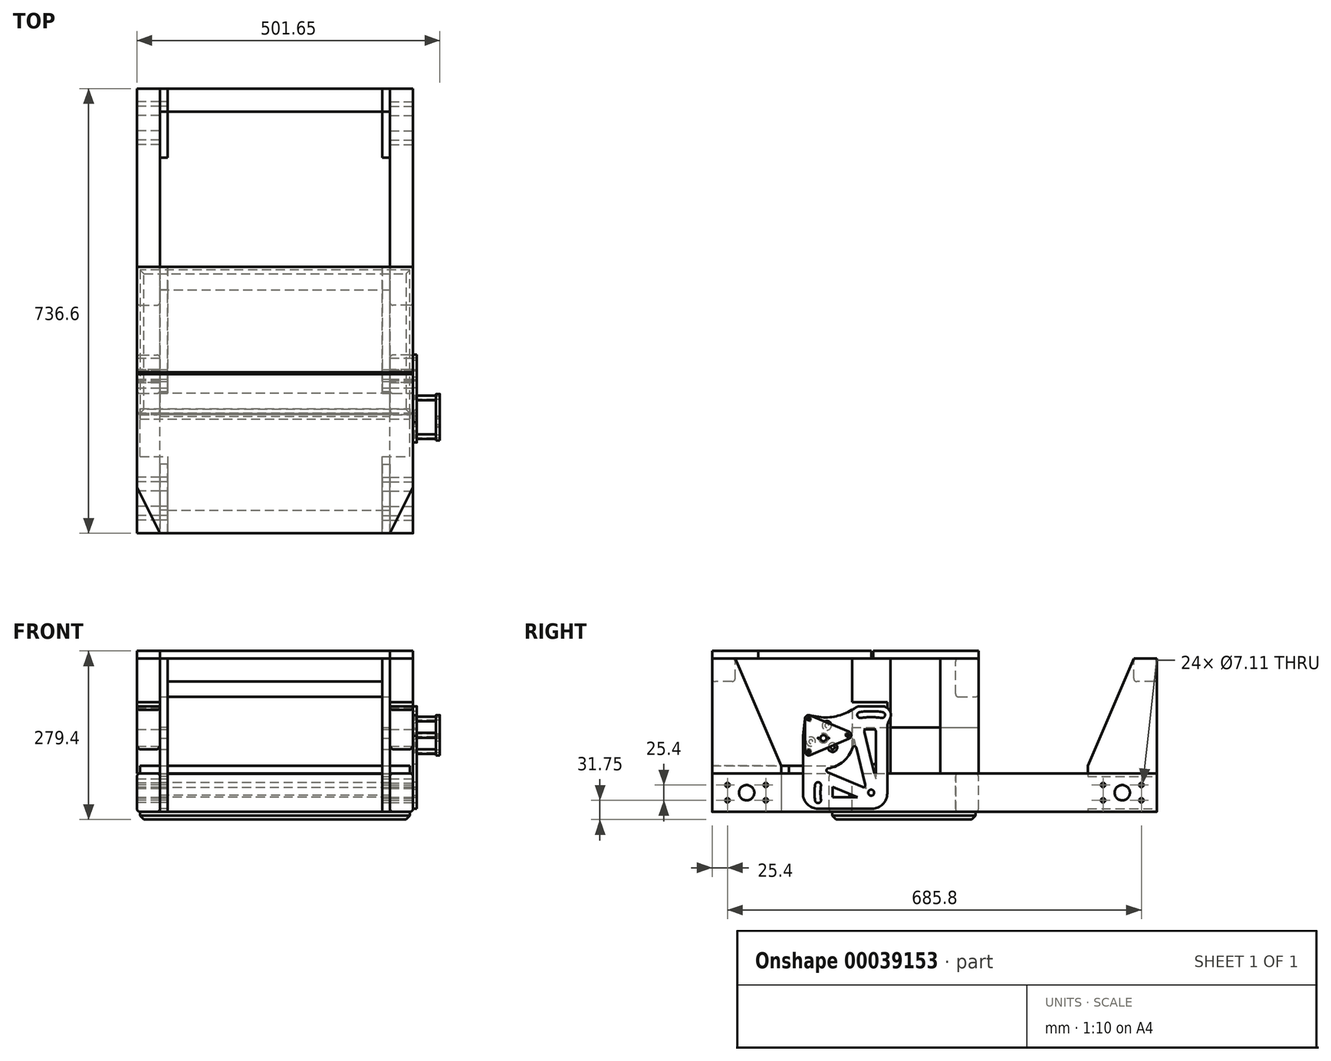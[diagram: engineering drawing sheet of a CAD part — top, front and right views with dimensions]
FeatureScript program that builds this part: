
annotation { "Feature Type Name" : "Feature", "Feature Type Description" : "" }
export const myFeature = defineFeature(function(context is Context, id is Id, definition is map)
    precondition{}
    {
        {
            var Q0;
            Q0=qCreatedBy(makeId("Front.planeOp"),FACE);
            var sketch = newSketch(context, id + "F0", { "sketchPlane" : qUnion([Q0])});
            skLineSegment(sketch, "E0", {"start": v(0, 25.4) * mm, "end": v(0, -25.4) * mm, "construction": true});
            skLineSegment(sketch, "E1.rect.bottom", {"start": v(-190.5, 31.75) * mm, "end": v(-228.6, 31.75) * mm});
            skLineSegment(sketch, "E1.rect.top", {"start": v(-190.5, -31.75) * mm, "end": v(-228.6, -31.75) * mm});
            skLineSegment(sketch, "E1.rect.left", {"start": v(-190.5, 31.75) * mm, "end": v(-190.5, -31.75) * mm});
            skLineSegment(sketch, "E1.rect.right", {"start": v(-228.6, 31.75) * mm, "end": v(-228.6, -31.75) * mm});
            skPoint(sketch, "E1.rect.middle", {"position": v(-209.55, 0) * mm});
            skLineSegment(sketch, "E2.MirrorCS", {"start": v(190.5, 31.75) * mm, "end": v(228.6, 31.75) * mm});
            skLineSegment(sketch, "E3.MirrorCS", {"start": v(190.5, -31.75) * mm, "end": v(228.6, -31.75) * mm});
            skLineSegment(sketch, "E4.MirrorCS", {"start": v(228.6, 31.75) * mm, "end": v(228.6, -31.75) * mm});
            skLineSegment(sketch, "E5.MirrorCS", {"start": v(190.5, 31.75) * mm, "end": v(190.5, -31.75) * mm});
            skPoint(sketch, "E6.MirrorP", {"position": v(209.55, 0) * mm});
            skSolve(sketch);
        }
        {
            var Q0;
            Q0=makeQuery(id+"F0.imprint","IMPRINT",FACE,{"disambiguationData":[TD([[makeQuery(id+"F0.imprint","IMPRINT",EDGE,{"derivedFrom":sQuery(id+"F0.wireOp",EDGE,"E1.rect.bottom")}),1.0]])]});
            extrude(context, id + "F1", {"entities" : qUnion([Q0]), "endBound" : BoundingType.SYMMETRIC, "depth" : 736.6 * mm});
        }
        {
            var Q0;
            Q0=makeQuery(id+"F1.opExtrude","SWEPT_FACE",FACE,{"disambiguationData":[OSD([sQuery(id+"F0.wireOp",EDGE,"E1.rect.right")])]});
            var sketch = newSketch(context, id + "F2", { "sketchPlane" : qUnion([Q0])});
            skLineSegment(sketch, "E7.rect.bottom", {"start": v(342.9, -12.7) * mm, "end": v(279.4, -12.7) * mm, "construction": true});
            skLineSegment(sketch, "E7.rect.top", {"start": v(342.9, 12.7) * mm, "end": v(279.4, 12.7) * mm, "construction": true});
            skLineSegment(sketch, "E7.rect.left", {"start": v(342.9, -12.7) * mm, "end": v(342.9, 12.7) * mm, "construction": true});
            skLineSegment(sketch, "E7.rect.right", {"start": v(279.4, -12.7) * mm, "end": v(279.4, 12.7) * mm, "construction": true});
            skPoint(sketch, "E7.rect.middle", {"position": v(311.15, 0) * mm});
            skCircle(sketch, "E8", {"center": v(311.15, 0) * mm, "radius": 12.7 * mm});
            skCircle(sketch, "E9", {"center": v(279.4, 12.7) * mm, "radius": 3.56 * mm});
            skCircle(sketch, "E10", {"center": v(279.4, -12.7) * mm, "radius": 3.56 * mm});
            skCircle(sketch, "E11", {"center": v(342.9, -12.7) * mm, "radius": 3.56 * mm});
            skCircle(sketch, "E12", {"center": v(342.9, 12.7) * mm, "radius": 3.56 * mm});
            skLineSegment(sketch, "E13", {"start": v(0, 31.75) * mm, "end": v(0, -31.75) * mm, "construction": true});
            skCircle(sketch, "E14.MirrorC", {"center": v(-342.9, 12.7) * mm, "radius": 3.56 * mm});
            skCircle(sketch, "E15.MirrorC", {"center": v(-342.9, -12.7) * mm, "radius": 3.56 * mm});
            skCircle(sketch, "E16.MirrorC", {"center": v(-279.4, 12.7) * mm, "radius": 3.56 * mm});
            skCircle(sketch, "E17.MirrorC", {"center": v(-279.4, -12.7) * mm, "radius": 3.56 * mm});
            skCircle(sketch, "E18.MirrorC", {"center": v(-311.15, 0) * mm, "radius": 12.7 * mm});
            skSolve(sketch);
        }
        {
            var Q0;
            Q0 = qSketchRegion(id + "F2", true);
            extrude(context, id + "F3", {"entities" : qUnion([Q0]), "operationType" : NewBodyOperationType.REMOVE, "endBound" : BoundingType.THROUGH_ALL, "oppositeDirection" : true, "depth" : 25.4 * mm});
        }
        {
            var Q0;
            Q0=makeQuery(id+"F1.opExtrude","SWEPT_EDGE",EDGE,{"disambiguationData":[OSD([sQuery(id+"F0.wireOp",EDGE,"E1.rect.bottom"),sQuery(id+"F0.wireOp",EDGE,"E1.rect.right")])]});
            var Q1;
            Q1=makeQuery(id+"F1.opExtrude","SWEPT_EDGE",EDGE,{"disambiguationData":[OSD([sQuery(id+"F0.wireOp",EDGE,"E1.rect.bottom"),sQuery(id+"F0.wireOp",EDGE,"E1.rect.left")])]});
            var Q2;
            Q2=makeQuery(id+"F1.opExtrude","SWEPT_EDGE",EDGE,{"disambiguationData":[OSD([sQuery(id+"F0.wireOp",EDGE,"E1.rect.top"),sQuery(id+"F0.wireOp",EDGE,"E1.rect.right")])]});
            var Q3;
            Q3=makeQuery(id+"F1.opExtrude","SWEPT_EDGE",EDGE,{"disambiguationData":[OSD([sQuery(id+"F0.wireOp",EDGE,"E1.rect.top"),sQuery(id+"F0.wireOp",EDGE,"E1.rect.left")])]});
            fillet(context, id + "F4", {"entities" : qUnion([Q0, Q1, Q2, Q3]), "radius" : 5.08 * mm, "tangentPropagation" : true, "allowEdgeOverflow" : false});
        }
        {
            var Q0;
            Q0=makeQuery(id+"F1.opExtrude","SWEPT_BODY",BODY,{"disambiguationData":[OSD([sQuery(id+"F0.wireOp",EDGE,"E1.rect.bottom"),sQuery(id+"F0.wireOp",EDGE,"E1.rect.top"),sQuery(id+"F0.wireOp",EDGE,"E1.rect.left"),sQuery(id+"F0.wireOp",EDGE,"E1.rect.right")])]});
            var Q1;
            Q1=qCreatedBy(makeId("Right.planeOp"),FACE);
            mirror(context, id + "F5", {"entities" : qUnion([Q0]), "mirrorPlane" : qUnion([Q1])});
        }
        {
            var Q0;
            Q0=makeQuery(id+"F1.opExtrude","SWEPT_FACE",FACE,{"disambiguationData":[OSD([sQuery(id+"F0.wireOp",EDGE,"E1.rect.bottom")])]});
            var sketch = newSketch(context, id + "F6", { "sketchPlane" : qUnion([Q0])});
            skLineSegment(sketch, "E19.bottom", {"start": v(-190.5, -174.62) * mm, "end": v(190.5, -174.62) * mm});
            skLineSegment(sketch, "E19.top", {"start": v(-190.5, -136.53) * mm, "end": v(190.5, -136.53) * mm});
            skLineSegment(sketch, "E19.left", {"start": v(-190.5, -174.62) * mm, "end": v(-190.5, -136.53) * mm});
            skLineSegment(sketch, "E19.right", {"start": v(190.5, -174.62) * mm, "end": v(190.5, -136.53) * mm});
            skLineSegment(sketch, "E20", {"start": v(-190.5, -50.8) * mm, "end": v(190.5, -50.8) * mm, "construction": true});
            skLineSegment(sketch, "E21.MirrorCS", {"start": v(-190.5, 73.02) * mm, "end": v(190.5, 73.02) * mm});
            skLineSegment(sketch, "E22.MirrorCS", {"start": v(-190.5, 34.92) * mm, "end": v(190.5, 34.92) * mm});
            skLineSegment(sketch, "E23.MirrorCS", {"start": v(190.5, 73.02) * mm, "end": v(190.5, 34.92) * mm});
            skLineSegment(sketch, "E24.MirrorCS", {"start": v(-190.5, 73.02) * mm, "end": v(-190.5, 34.92) * mm});
            skSolve(sketch);
        }
        {
            var Q0;
            Q0 = qSketchRegion(id + "F6", true);
            var Q1;
            Q1=makeQuery(id+"F5.opPattern","COPY",FACE,{"derivedFrom":makeQuery(id+"F1.opExtrude","SWEPT_FACE",FACE,{"disambiguationData":[OSD([sQuery(id+"F0.wireOp",EDGE,"E1.rect.top")])]}),"instanceName":"1"});
            extrude(context, id + "F7", {"entities" : qUnion([Q0]), "endBound" : BoundingType.UP_TO_SURFACE, "oppositeDirection" : true, "endBoundEntityFace" : qUnion([Q1]), "depth" : 25.4 * mm});
        }
        {
            var Q0;
            Q0=makeQuery(id+"F7.opExtrude","CAP_EDGE",EDGE,{"disambiguationData":[OSD([sQuery(id+"F6.wireOp",EDGE,"E21.MirrorCS")])],"isStart":false});
            var Q1;
            Q1=makeQuery(id+"F7.opExtrude","CAP_EDGE",EDGE,{"disambiguationData":[OSD([sQuery(id+"F6.wireOp",EDGE,"E22.MirrorCS")])],"isStart":false});
            var Q2;
            Q2=makeQuery(id+"F7.opExtrude","CAP_EDGE",EDGE,{"disambiguationData":[OSD([sQuery(id+"F6.wireOp",EDGE,"E19.top")])],"isStart":false});
            var Q3;
            Q3=makeQuery(id+"F7.opExtrude","CAP_EDGE",EDGE,{"disambiguationData":[OSD([sQuery(id+"F6.wireOp",EDGE,"E19.bottom")])],"isStart":false});
            var Q4;
            Q4=makeQuery(id+"F7.opExtrude","CAP_EDGE",EDGE,{"disambiguationData":[OSD([sQuery(id+"F6.wireOp",EDGE,"E19.bottom")])],"isStart":true});
            var Q5;
            Q5=makeQuery(id+"F7.opExtrude","CAP_EDGE",EDGE,{"disambiguationData":[OSD([sQuery(id+"F6.wireOp",EDGE,"E19.top")])],"isStart":true});
            var Q6;
            Q6=makeQuery(id+"F7.opExtrude","CAP_EDGE",EDGE,{"disambiguationData":[OSD([sQuery(id+"F6.wireOp",EDGE,"E22.MirrorCS")])],"isStart":true});
            var Q7;
            Q7=makeQuery(id+"F7.opExtrude","CAP_EDGE",EDGE,{"disambiguationData":[OSD([sQuery(id+"F6.wireOp",EDGE,"E21.MirrorCS")])],"isStart":true});
            fillet(context, id + "F8", {"entities" : qUnion([Q0, Q1, Q2, Q3, Q4, Q5, Q6, Q7]), "radius" : 5.08 * mm, "tangentPropagation" : true, "allowEdgeOverflow" : false});
        }
        {
            var Q0;
            Q0=makeQuery(id+"F1.opExtrude","SWEPT_FACE",FACE,{"disambiguationData":[OSD([sQuery(id+"F0.wireOp",EDGE,"E1.rect.bottom")])]});
            var sketch = newSketch(context, id + "F9", { "sketchPlane" : qUnion([Q0])});
            skLineSegment(sketch, "E25.bottom", {"start": v(-223.52, -241.3) * mm, "end": v(-177.8, -241.3) * mm});
            skLineSegment(sketch, "E25.top", {"start": v(-223.52, -141.6) * mm, "end": v(223.52, -141.6) * mm});
            skLineSegment(sketch, "E25.left", {"start": v(-223.52, -241.3) * mm, "end": v(-223.52, -141.6) * mm});
            skLineSegment(sketch, "E25.right", {"start": v(223.52, -241.3) * mm, "end": v(223.52, -141.6) * mm});
            skLineSegment(sketch, "E26.0", {"start": v(190.5, -141.6) * mm, "end": v(-190.5, -141.6) * mm, "construction": true});
            skLineSegment(sketch, "E27", {"start": v(-177.8, -241.3) * mm, "end": v(-177.8, -368.3) * mm});
            skLineSegment(sketch, "E28", {"start": v(-177.8, -368.3) * mm, "end": v(177.8, -368.3) * mm});
            skLineSegment(sketch, "E29", {"start": v(177.8, -368.3) * mm, "end": v(177.8, -241.3) * mm});
            skLineSegment(sketch, "E30", {"start": v(0, -141.6) * mm, "end": v(0, -368.3) * mm, "construction": true});
            skLineSegment(sketch, "E31.trimOffspring", {"start": v(177.8, -241.3) * mm, "end": v(223.52, -241.3) * mm});
            skSolve(sketch);
        }
        {
            var Q0;
            Q0 = qSketchRegion(id + "F9", true);
            extrude(context, id + "F10", {"entities" : qUnion([Q0]), "depth" : 12.7 * mm});
        }
        {
            var Q0;
            Q0=makeQuery(id+"F5.opPattern","COPY",FACE,{"derivedFrom":makeQuery(id+"F1.opExtrude","SWEPT_FACE",FACE,{"disambiguationData":[OSD([sQuery(id+"F0.wireOp",EDGE,"E1.rect.top")])]}),"instanceName":"1"});
            var sketch = newSketch(context, id + "F11", { "sketchPlane" : qUnion([Q0])});
            skLineSegment(sketch, "E32.bottom", {"start": v(223.52, 169.55) * mm, "end": v(-223.52, 169.54) * mm});
            skLineSegment(sketch, "E32.top", {"start": v(223.52, -67.94) * mm, "end": v(-223.52, -67.95) * mm});
            skLineSegment(sketch, "E32.left", {"start": v(223.52, 169.55) * mm, "end": v(223.52, -67.94) * mm});
            skLineSegment(sketch, "E32.right", {"start": v(-223.52, 169.54) * mm, "end": v(-223.52, -67.95) * mm});
            skSolve(sketch);
        }
        {
            var Q0;
            Q0 = qSketchRegion(id + "F11", true);
            extrude(context, id + "F12", {"entities" : qUnion([Q0]), "depth" : 12.7 * mm});
        }
        {
            var Q0;
            Q0=makeQuery(id+"F12.opExtrude","CAP_EDGE",EDGE,{"disambiguationData":[OSD([sQuery(id+"F11.wireOp",EDGE,"E32.top")])],"isStart":false});
            var Q1;
            Q1=makeQuery(id+"F12.opExtrude","CAP_EDGE",EDGE,{"disambiguationData":[OSD([sQuery(id+"F11.wireOp",EDGE,"E32.left")])],"isStart":false});
            var Q2;
            Q2=makeQuery(id+"F12.opExtrude","CAP_EDGE",EDGE,{"disambiguationData":[OSD([sQuery(id+"F11.wireOp",EDGE,"E32.bottom")])],"isStart":false});
            var Q3;
            Q3=makeQuery(id+"F12.opExtrude","CAP_EDGE",EDGE,{"disambiguationData":[OSD([sQuery(id+"F11.wireOp",EDGE,"E32.right")])],"isStart":false});
            chamfer(context, id + "F13", {"entities" : qUnion([Q0, Q1, Q2, Q3]), "width" : 6.35 * mm, "tangentPropagation" : true});
        }
        {
            var Q0;
            Q0=makeQuery(id+"F1.opExtrude","SWEPT_FACE",FACE,{"disambiguationData":[OSD([sQuery(id+"F0.wireOp",EDGE,"E1.rect.left")])]});
            var sketch = newSketch(context, id + "F14", { "sketchPlane" : qUnion([Q0])});
            skLineSegment(sketch, "E33", {"start": v(-254, -31.75) * mm, "end": v(-368.3, -31.75) * mm});
            skPoint(sketch, "E33.endSnap0", {"position": v(-368.3, 0) * mm});
            skLineSegment(sketch, "E34", {"start": v(-368.3, -31.75) * mm, "end": v(-368.3, 222.25) * mm});
            skLineSegment(sketch, "E35", {"start": v(-368.3, 222.25) * mm, "end": v(-330.2, 222.25) * mm});
            skLineSegment(sketch, "E36", {"start": v(-330.2, 222.25) * mm, "end": v(-254, 44.45) * mm});
            skLineSegment(sketch, "E37", {"start": v(-254, 44.45) * mm, "end": v(-254, -31.75) * mm});
            skLineSegment(sketch, "E38", {"start": v(0, -26.67) * mm, "end": v(0, 26.67) * mm, "construction": true});
            skLineSegment(sketch, "E39.MirrorCS", {"start": v(368.3, 222.25) * mm, "end": v(330.2, 222.25) * mm});
            skLineSegment(sketch, "E40.MirrorCS", {"start": v(254, -31.75) * mm, "end": v(368.3, -31.75) * mm});
            skPoint(sketch, "E41.MirrorP", {"position": v(368.3, 0) * mm});
            skLineSegment(sketch, "E42.MirrorCS", {"start": v(330.2, 222.25) * mm, "end": v(254, 44.45) * mm});
            skLineSegment(sketch, "E43.MirrorCS", {"start": v(254, 44.45) * mm, "end": v(254, -31.75) * mm});
            skLineSegment(sketch, "E44.MirrorCS", {"start": v(368.3, -31.75) * mm, "end": v(368.3, 222.25) * mm});
            skSolve(sketch);
        }
        {
            var Q0;
            {var subQ6=sQuery(id+"F14.wireOp",EDGE,"E35");Q0=makeQuery(id+"F14.imprint","IMPRINT",FACE,{"disambiguationData":[TD([[makeQuery(id+"F14.imprint","IMPRINT",EDGE,{"derivedFrom":subQ6}),-1.0]])]});}
            var Q1;
            {var subQ0=sQuery(id+"F0.wireOp",EDGE,"E1.rect.left");var subQ1=makeQuery(id+"F1.opExtrude","SWEPT_FACE",FACE,{"disambiguationData":[OSD([subQ0])]});Q1=makeQuery(id+"F14.imprint","IMPRINT",FACE,{"disambiguationData":[TD([[makeQuery(id+"F14.imprint","IMPRINT",EDGE,{"derivedFrom":makeQuery(id+"F3.boolean.opBoolean","INTERSECT",EDGE,{"derivedFrom":[subQ1,makeQuery(id+"F3.opExtrude","SWEPT_FACE",FACE,{"disambiguationData":[OSD([sQuery(id+"F2.wireOp",EDGE,"E8")])]})]})}),-1.0]])]});}
            var Q2;
            {var subQ4=sQuery(id+"F14.wireOp",EDGE,"E33");Q2=makeQuery(id+"F14.imprint","IMPRINT",FACE,{"disambiguationData":[TD([[makeQuery(id+"F14.imprint","IMPRINT",EDGE,{"derivedFrom":subQ4}),-1.0]])]});}
            var Q3;
            {var subQ0=sQuery(id+"F14.wireOp",EDGE,"E39.MirrorCS");Q3=makeQuery(id+"F14.imprint","IMPRINT",FACE,{"disambiguationData":[TD([[makeQuery(id+"F14.imprint","IMPRINT",EDGE,{"derivedFrom":subQ0}),1.0]])]});}
            var Q4;
            {var subQ0=sQuery(id+"F0.wireOp",EDGE,"E1.rect.left");var subQ1=makeQuery(id+"F1.opExtrude","SWEPT_FACE",FACE,{"disambiguationData":[OSD([subQ0])]});Q4=makeQuery(id+"F14.imprint","IMPRINT",FACE,{"disambiguationData":[TD([[makeQuery(id+"F14.imprint","IMPRINT",EDGE,{"derivedFrom":makeQuery(id+"F3.boolean.opBoolean","INTERSECT",EDGE,{"derivedFrom":[subQ1,makeQuery(id+"F3.opExtrude","SWEPT_FACE",FACE,{"disambiguationData":[OSD([sQuery(id+"F2.wireOp",EDGE,"E14.MirrorC")])]})]})}),1.0]])]});}
            var Q5;
            {var subQ6=sQuery(id+"F14.wireOp",EDGE,"E40.MirrorCS");Q5=makeQuery(id+"F14.imprint","IMPRINT",FACE,{"disambiguationData":[TD([[makeQuery(id+"F14.imprint","IMPRINT",EDGE,{"derivedFrom":subQ6}),1.0]])]});}
            extrude(context, id + "F15", {"entities" : qUnion([Q0, Q1, Q2, Q3, Q4, Q5]), "depth" : 12.7 * mm});
        }
        {
            var Q0;
            Q0=makeQuery(id+"F1.opExtrude","SWEPT_FACE",FACE,{"disambiguationData":[OSD([sQuery(id+"F0.wireOp",EDGE,"E1.rect.bottom")])]});
            var sketch = newSketch(context, id + "F16", { "sketchPlane" : qUnion([Q0])});
            skLineSegment(sketch, "E45.bottom", {"start": v(-228.6, 73.02) * mm, "end": v(-190.5, 73.02) * mm});
            skLineSegment(sketch, "E45.top", {"start": v(-228.6, 9.52) * mm, "end": v(-190.5, 9.52) * mm});
            skLineSegment(sketch, "E45.left", {"start": v(-228.6, 73.02) * mm, "end": v(-228.6, 9.52) * mm});
            skLineSegment(sketch, "E45.right", {"start": v(-190.5, 73.02) * mm, "end": v(-190.5, 9.52) * mm});
            skLineSegment(sketch, "E46.bottom", {"start": v(-228.6, -136.53) * mm, "end": v(-190.5, -136.53) * mm});
            skLineSegment(sketch, "E46.top", {"start": v(-228.6, -73.03) * mm, "end": v(-190.5, -73.03) * mm});
            skLineSegment(sketch, "E46.left", {"start": v(-228.6, -136.53) * mm, "end": v(-228.6, -73.03) * mm});
            skLineSegment(sketch, "E46.right", {"start": v(-190.5, -136.53) * mm, "end": v(-190.5, -73.03) * mm});
            skSolve(sketch);
        }
        {
            var Q0;
            Q0 = qSketchRegion(id + "F16", true);
            var Q1;
            Q1=makeQuery(id+"F15.opExtrude","SWEPT_FACE",FACE,{"disambiguationData":[OSD([sQuery(id+"F14.wireOp",EDGE,"E35")])]});
            extrude(context, id + "F17", {"entities" : qUnion([Q0]), "endBound" : BoundingType.UP_TO_SURFACE, "endBoundEntityFace" : qUnion([Q1]), "depth" : 25.4 * mm});
        }
        {
            var Q0;
            Q0=makeQuery(id+"F1.opExtrude","SWEPT_FACE",FACE,{"disambiguationData":[OSD([sQuery(id+"F0.wireOp",EDGE,"E1.rect.left")])]});
            var sketch = newSketch(context, id + "F18", { "sketchPlane" : qUnion([Q0])});
            skLineSegment(sketch, "E47", {"start": v(-136.53, -31.75) * mm, "end": v(-136.53, 107.95) * mm});
            skLineSegment(sketch, "E48", {"start": v(-136.53, 107.95) * mm, "end": v(73.02, 107.95) * mm});
            skLineSegment(sketch, "E49", {"start": v(73.02, 107.95) * mm, "end": v(73.02, 31.75) * mm});
            skLineSegment(sketch, "E50", {"start": v(73.02, 31.75) * mm, "end": v(34.92, 31.75) * mm});
            skLineSegment(sketch, "E51", {"start": v(34.92, 31.75) * mm, "end": v(34.92, -31.75) * mm});
            skLineSegment(sketch, "E52", {"start": v(34.92, -31.75) * mm, "end": v(-136.53, -31.75) * mm});
            skSolve(sketch);
        }
        {
            var Q0;
            Q0 = qSketchRegion(id + "F18", true);
            extrude(context, id + "F19", {"entities" : qUnion([Q0]), "depth" : 12.7 * mm});
        }
        {
            var Q0;
            Q0=makeQuery(id+"F15.opExtrude","SWEPT_BODY",BODY,{"disambiguationData":[OSD([sQuery(id+"F0.wireOp",EDGE,"E1.rect.left"),sQuery(id+"F2.wireOp",EDGE,"E8"),sQuery(id+"F2.wireOp",EDGE,"E9"),sQuery(id+"F2.wireOp",EDGE,"E10"),sQuery(id+"F2.wireOp",EDGE,"E11"),sQuery(id+"F2.wireOp",EDGE,"E12"),sQuery(id+"F14.wireOp",EDGE,"E33"),sQuery(id+"F14.wireOp",EDGE,"E34"),sQuery(id+"F14.wireOp",EDGE,"E35"),sQuery(id+"F14.wireOp",EDGE,"E36"),sQuery(id+"F14.wireOp",EDGE,"E37")])]});
            var Q1;
            Q1=makeQuery(id+"F17.opExtrude","SWEPT_BODY",BODY,{"disambiguationData":[OSD([sQuery(id+"F16.wireOp",EDGE,"E46.bottom"),sQuery(id+"F16.wireOp",EDGE,"E46.top"),sQuery(id+"F16.wireOp",EDGE,"E46.left"),sQuery(id+"F16.wireOp",EDGE,"E46.right")])]});
            var Q2;
            Q2=makeQuery(id+"F19.opExtrude","SWEPT_BODY",BODY,{"disambiguationData":[OSD([sQuery(id+"F18.wireOp",EDGE,"E47"),sQuery(id+"F18.wireOp",EDGE,"E48"),sQuery(id+"F18.wireOp",EDGE,"E49"),sQuery(id+"F18.wireOp",EDGE,"E50"),sQuery(id+"F18.wireOp",EDGE,"E51"),sQuery(id+"F18.wireOp",EDGE,"E52")])]});
            var Q3;
            Q3=makeQuery(id+"F17.opExtrude","SWEPT_BODY",BODY,{"disambiguationData":[OSD([sQuery(id+"F16.wireOp",EDGE,"E45.bottom"),sQuery(id+"F16.wireOp",EDGE,"E45.top"),sQuery(id+"F16.wireOp",EDGE,"E45.left"),sQuery(id+"F16.wireOp",EDGE,"E45.right")])]});
            var Q4;
            Q4=makeQuery(id+"F15.opExtrude","SWEPT_BODY",BODY,{"disambiguationData":[OSD([sQuery(id+"F0.wireOp",EDGE,"E1.rect.left"),sQuery(id+"F2.wireOp",EDGE,"E14.MirrorC"),sQuery(id+"F2.wireOp",EDGE,"E15.MirrorC"),sQuery(id+"F2.wireOp",EDGE,"E16.MirrorC"),sQuery(id+"F2.wireOp",EDGE,"E17.MirrorC"),sQuery(id+"F2.wireOp",EDGE,"E18.MirrorC"),sQuery(id+"F14.wireOp",EDGE,"E39.MirrorCS"),sQuery(id+"F14.wireOp",EDGE,"E40.MirrorCS"),sQuery(id+"F14.wireOp",EDGE,"E42.MirrorCS"),sQuery(id+"F14.wireOp",EDGE,"E43.MirrorCS"),sQuery(id+"F14.wireOp",EDGE,"E44.MirrorCS")])]});
            var Q5;
            Q5=qCreatedBy(makeId("Right.planeOp"),FACE);
            mirror(context, id + "F20", {"entities" : qUnion([Q0, Q1, Q2, Q3, Q4]), "mirrorPlane" : qUnion([Q5])});
        }
        {
            var Q0;
            Q0=makeQuery(id+"F20.opPattern","COPY",FACE,{"derivedFrom":makeQuery(id+"F15.opExtrude","CAP_FACE",FACE,{"disambiguationData":[OSD([sQuery(id+"F0.wireOp",EDGE,"E1.rect.left"),sQuery(id+"F2.wireOp",EDGE,"E14.MirrorC"),sQuery(id+"F2.wireOp",EDGE,"E15.MirrorC"),sQuery(id+"F2.wireOp",EDGE,"E16.MirrorC"),sQuery(id+"F2.wireOp",EDGE,"E17.MirrorC"),sQuery(id+"F2.wireOp",EDGE,"E18.MirrorC"),sQuery(id+"F14.wireOp",EDGE,"E39.MirrorCS"),sQuery(id+"F14.wireOp",EDGE,"E40.MirrorCS"),sQuery(id+"F14.wireOp",EDGE,"E42.MirrorCS"),sQuery(id+"F14.wireOp",EDGE,"E43.MirrorCS"),sQuery(id+"F14.wireOp",EDGE,"E44.MirrorCS")])],"isStart":false}),"instanceName":"1"});
            var sketch = newSketch(context, id + "F21", { "sketchPlane" : qUnion([Q0])});
            skLineSegment(sketch, "E53.bottom", {"start": v(-330.2, 222.25) * mm, "end": v(-368.3, 222.25) * mm});
            skLineSegment(sketch, "E53.top", {"start": v(-330.2, 184.15) * mm, "end": v(-368.3, 184.15) * mm});
            skLineSegment(sketch, "E53.left", {"start": v(-330.2, 222.25) * mm, "end": v(-330.2, 184.15) * mm});
            skLineSegment(sketch, "E53.right", {"start": v(-368.3, 222.25) * mm, "end": v(-368.3, 184.15) * mm});
            skLineSegment(sketch, "E54.bottom", {"start": v(368.3, 222.25) * mm, "end": v(330.2, 222.25) * mm});
            skLineSegment(sketch, "E54.top", {"start": v(368.3, 184.15) * mm, "end": v(330.2, 184.15) * mm});
            skLineSegment(sketch, "E54.left", {"start": v(368.3, 222.25) * mm, "end": v(368.3, 184.15) * mm});
            skLineSegment(sketch, "E54.right", {"start": v(330.2, 222.25) * mm, "end": v(330.2, 184.15) * mm});
            skSolve(sketch);
        }
        {
            var Q0;
            Q0 = qSketchRegion(id + "F21", true);
            var Q1;
            Q1=makeQuery(id+"F15.opExtrude","CAP_FACE",FACE,{"disambiguationData":[OSD([sQuery(id+"F0.wireOp",EDGE,"E1.rect.left"),sQuery(id+"F2.wireOp",EDGE,"E14.MirrorC"),sQuery(id+"F2.wireOp",EDGE,"E15.MirrorC"),sQuery(id+"F2.wireOp",EDGE,"E16.MirrorC"),sQuery(id+"F2.wireOp",EDGE,"E17.MirrorC"),sQuery(id+"F2.wireOp",EDGE,"E18.MirrorC"),sQuery(id+"F14.wireOp",EDGE,"E39.MirrorCS"),sQuery(id+"F14.wireOp",EDGE,"E40.MirrorCS"),sQuery(id+"F14.wireOp",EDGE,"E42.MirrorCS"),sQuery(id+"F14.wireOp",EDGE,"E43.MirrorCS"),sQuery(id+"F14.wireOp",EDGE,"E44.MirrorCS")])],"isStart":false});
            extrude(context, id + "F22", {"entities" : qUnion([Q0]), "endBound" : BoundingType.UP_TO_SURFACE, "endBoundEntityFace" : qUnion([Q1]), "depth" : 25.4 * mm});
        }
        {
            var Q0;
            Q0=makeQuery(id+"F20.opPattern","COPY",FACE,{"derivedFrom":makeQuery(id+"F17.opExtrude","SWEPT_FACE",FACE,{"disambiguationData":[OSD([sQuery(id+"F16.wireOp",EDGE,"E45.right")])]}),"instanceName":"1"});
            var sketch = newSketch(context, id + "F23", { "sketchPlane" : qUnion([Q0])});
            skLineSegment(sketch, "E55.bottom", {"start": v(-73.02, 222.25) * mm, "end": v(-34.92, 222.25) * mm});
            skLineSegment(sketch, "E55.top", {"start": v(-73.02, 158.75) * mm, "end": v(-34.92, 158.75) * mm});
            skLineSegment(sketch, "E55.left", {"start": v(-73.02, 222.25) * mm, "end": v(-73.02, 158.75) * mm});
            skLineSegment(sketch, "E55.right", {"start": v(-34.92, 222.25) * mm, "end": v(-34.92, 158.75) * mm});
            skSolve(sketch);
        }
        {
            var Q0;
            Q0 = qSketchRegion(id + "F23", true);
            var Q1;
            Q1=makeQuery(id+"F17.opExtrude","SWEPT_FACE",FACE,{"disambiguationData":[OSD([sQuery(id+"F16.wireOp",EDGE,"E45.right")])]});
            extrude(context, id + "F24", {"entities" : qUnion([Q0]), "endBound" : BoundingType.UP_TO_SURFACE, "endBoundEntityFace" : qUnion([Q1]), "depth" : 25.4 * mm});
        }
        {
            var Q0;
            Q0=makeQuery(id+"F22.opExtrude","SWEPT_EDGE",EDGE,{"disambiguationData":[OSD([sQuery(id+"F14.wireOp",EDGE,"E42.MirrorCS"),sQuery(id+"F21.wireOp",EDGE,"E53.bottom"),sQuery(id+"F21.wireOp",EDGE,"E53.left")])]});
            var Q1;
            Q1=makeQuery(id+"F22.opExtrude","SWEPT_EDGE",EDGE,{"disambiguationData":[OSD([sQuery(id+"F21.wireOp",EDGE,"E53.bottom"),sQuery(id+"F21.wireOp",EDGE,"E53.right")])]});
            var Q2;
            Q2=makeQuery(id+"F22.opExtrude","SWEPT_EDGE",EDGE,{"disambiguationData":[OSD([sQuery(id+"F21.wireOp",EDGE,"E53.top"),sQuery(id+"F21.wireOp",EDGE,"E53.left")])]});
            var Q3;
            Q3=makeQuery(id+"F22.opExtrude","SWEPT_EDGE",EDGE,{"disambiguationData":[OSD([sQuery(id+"F14.wireOp",EDGE,"E44.MirrorCS"),sQuery(id+"F21.wireOp",EDGE,"E53.top"),sQuery(id+"F21.wireOp",EDGE,"E53.right")])]});
            var Q4;
            Q4=makeQuery(id+"F24.opExtrude","SWEPT_EDGE",EDGE,{"disambiguationData":[OSD([sQuery(id+"F23.wireOp",EDGE,"E55.bottom"),sQuery(id+"F23.wireOp",EDGE,"E55.left")])]});
            var Q5;
            Q5=makeQuery(id+"F24.opExtrude","SWEPT_EDGE",EDGE,{"disambiguationData":[OSD([sQuery(id+"F16.wireOp",EDGE,"E45.bottom"),sQuery(id+"F16.wireOp",EDGE,"E45.right"),sQuery(id+"F23.wireOp",EDGE,"E55.top"),sQuery(id+"F23.wireOp",EDGE,"E55.left")])]});
            var Q6;
            Q6=makeQuery(id+"F24.opExtrude","SWEPT_EDGE",EDGE,{"disambiguationData":[OSD([sQuery(id+"F16.wireOp",EDGE,"E45.right"),sQuery(id+"F23.wireOp",EDGE,"E55.bottom"),sQuery(id+"F23.wireOp",EDGE,"E55.right")])]});
            var Q7;
            Q7=makeQuery(id+"F24.opExtrude","SWEPT_EDGE",EDGE,{"disambiguationData":[OSD([sQuery(id+"F23.wireOp",EDGE,"E55.top"),sQuery(id+"F23.wireOp",EDGE,"E55.right")])]});
            var Q8;
            Q8=makeQuery(id+"F17.opExtrude","SWEPT_EDGE",EDGE,{"disambiguationData":[OSD([sQuery(id+"F16.wireOp",EDGE,"E45.top"),sQuery(id+"F16.wireOp",EDGE,"E45.right")])]});
            var Q9;
            Q9=makeQuery(id+"F17.opExtrude","SWEPT_EDGE",EDGE,{"disambiguationData":[OSD([sQuery(id+"F16.wireOp",EDGE,"E45.top"),sQuery(id+"F16.wireOp",EDGE,"E45.left")])]});
            var Q10;
            Q10=makeQuery(id+"F17.opExtrude","SWEPT_EDGE",EDGE,{"disambiguationData":[OSD([sQuery(id+"F16.wireOp",EDGE,"E45.bottom"),sQuery(id+"F16.wireOp",EDGE,"E45.left")])]});
            var Q11;
            Q11=makeQuery(id+"F17.opExtrude","SWEPT_EDGE",EDGE,{"disambiguationData":[OSD([sQuery(id+"F16.wireOp",EDGE,"E45.bottom"),sQuery(id+"F16.wireOp",EDGE,"E45.right")])]});
            var Q12;
            Q12=makeQuery(id+"F17.opExtrude","SWEPT_EDGE",EDGE,{"disambiguationData":[OSD([sQuery(id+"F16.wireOp",EDGE,"E46.top"),sQuery(id+"F16.wireOp",EDGE,"E46.right")])]});
            var Q13;
            Q13=makeQuery(id+"F17.opExtrude","SWEPT_EDGE",EDGE,{"disambiguationData":[OSD([sQuery(id+"F16.wireOp",EDGE,"E46.top"),sQuery(id+"F16.wireOp",EDGE,"E46.left")])]});
            var Q14;
            Q14=makeQuery(id+"F17.opExtrude","SWEPT_EDGE",EDGE,{"disambiguationData":[OSD([sQuery(id+"F16.wireOp",EDGE,"E46.bottom"),sQuery(id+"F16.wireOp",EDGE,"E46.left")])]});
            var Q15;
            Q15=makeQuery(id+"F17.opExtrude","SWEPT_EDGE",EDGE,{"disambiguationData":[OSD([sQuery(id+"F16.wireOp",EDGE,"E46.bottom"),sQuery(id+"F16.wireOp",EDGE,"E46.right")])]});
            var Q16;
            Q16=makeQuery(id+"F20.opPattern","COPY",EDGE,{"derivedFrom":makeQuery(id+"F17.opExtrude","SWEPT_EDGE",EDGE,{"disambiguationData":[OSD([sQuery(id+"F16.wireOp",EDGE,"E46.bottom"),sQuery(id+"F16.wireOp",EDGE,"E46.right")])]}),"instanceName":"1"});
            var Q17;
            Q17=makeQuery(id+"F20.opPattern","COPY",EDGE,{"derivedFrom":makeQuery(id+"F17.opExtrude","SWEPT_EDGE",EDGE,{"disambiguationData":[OSD([sQuery(id+"F16.wireOp",EDGE,"E46.top"),sQuery(id+"F16.wireOp",EDGE,"E46.right")])]}),"instanceName":"1"});
            var Q18;
            Q18=makeQuery(id+"F20.opPattern","COPY",EDGE,{"derivedFrom":makeQuery(id+"F17.opExtrude","SWEPT_EDGE",EDGE,{"disambiguationData":[OSD([sQuery(id+"F16.wireOp",EDGE,"E46.bottom"),sQuery(id+"F16.wireOp",EDGE,"E46.left")])]}),"instanceName":"1"});
            var Q19;
            Q19=makeQuery(id+"F22.opExtrude","SWEPT_EDGE",EDGE,{"disambiguationData":[OSD([sQuery(id+"F21.wireOp",EDGE,"E54.bottom"),sQuery(id+"F21.wireOp",EDGE,"E54.left")])]});
            var Q20;
            Q20=makeQuery(id+"F22.opExtrude","SWEPT_EDGE",EDGE,{"disambiguationData":[OSD([sQuery(id+"F21.wireOp",EDGE,"E54.top"),sQuery(id+"F21.wireOp",EDGE,"E54.left")])]});
            var Q21;
            Q21=makeQuery(id+"F22.opExtrude","SWEPT_EDGE",EDGE,{"disambiguationData":[OSD([sQuery(id+"F21.wireOp",EDGE,"E54.bottom"),sQuery(id+"F21.wireOp",EDGE,"E54.right")])]});
            var Q22;
            Q22=makeQuery(id+"F22.opExtrude","SWEPT_EDGE",EDGE,{"disambiguationData":[OSD([sQuery(id+"F21.wireOp",EDGE,"E54.top"),sQuery(id+"F21.wireOp",EDGE,"E54.right")])]});
            var Q23;
            Q23=makeQuery(id+"F20.opPattern","COPY",EDGE,{"derivedFrom":makeQuery(id+"F17.opExtrude","SWEPT_EDGE",EDGE,{"disambiguationData":[OSD([sQuery(id+"F16.wireOp",EDGE,"E46.top"),sQuery(id+"F16.wireOp",EDGE,"E46.left")])]}),"instanceName":"1"});
            var Q24;
            Q24=makeQuery(id+"F20.opPattern","COPY",EDGE,{"derivedFrom":makeQuery(id+"F17.opExtrude","SWEPT_EDGE",EDGE,{"disambiguationData":[OSD([sQuery(id+"F16.wireOp",EDGE,"E45.bottom"),sQuery(id+"F16.wireOp",EDGE,"E45.left")])]}),"instanceName":"1"});
            var Q25;
            Q25=makeQuery(id+"F20.opPattern","COPY",EDGE,{"derivedFrom":makeQuery(id+"F17.opExtrude","SWEPT_EDGE",EDGE,{"disambiguationData":[OSD([sQuery(id+"F16.wireOp",EDGE,"E45.bottom"),sQuery(id+"F16.wireOp",EDGE,"E45.right")])]}),"instanceName":"1"});
            var Q26;
            Q26=makeQuery(id+"F20.opPattern","COPY",EDGE,{"derivedFrom":makeQuery(id+"F17.opExtrude","SWEPT_EDGE",EDGE,{"disambiguationData":[OSD([sQuery(id+"F16.wireOp",EDGE,"E45.top"),sQuery(id+"F16.wireOp",EDGE,"E45.left")])]}),"instanceName":"1"});
            var Q27;
            Q27=makeQuery(id+"F20.opPattern","COPY",EDGE,{"derivedFrom":makeQuery(id+"F17.opExtrude","SWEPT_EDGE",EDGE,{"disambiguationData":[OSD([sQuery(id+"F16.wireOp",EDGE,"E45.top"),sQuery(id+"F16.wireOp",EDGE,"E45.right")])]}),"instanceName":"1"});
            fillet(context, id + "F25", {"entities" : qUnion([Q0, Q1, Q2, Q3, Q4, Q5, Q6, Q7, Q8, Q9, Q10, Q11, Q12, Q13, Q14, Q15, Q16, Q17, Q18, Q19, Q20, Q21, Q22, Q23, Q24, Q25, Q26, Q27]), "radius" : 5.08 * mm, "tangentPropagation" : true, "allowEdgeOverflow" : false});
        }
        {
            var Q0;
            Q0=makeQuery(id+"F17.opExtrude","CAP_FACE",FACE,{"disambiguationData":[OSD([sQuery(id+"F16.wireOp",EDGE,"E46.bottom"),sQuery(id+"F16.wireOp",EDGE,"E46.top"),sQuery(id+"F16.wireOp",EDGE,"E46.left"),sQuery(id+"F16.wireOp",EDGE,"E46.right")])],"isStart":false});
            var sketch = newSketch(context, id + "F26", { "sketchPlane" : qUnion([Q0])});
            skLineSegment(sketch, "E56", {"start": v(228.6, -104.78) * mm, "end": v(228.6, -292.1) * mm});
            skLineSegment(sketch, "E57", {"start": v(228.6, -292.1) * mm, "end": v(190.5, -368.3) * mm});
            skLineSegment(sketch, "E58", {"start": v(190.5, -368.3) * mm, "end": v(-190.5, -368.3) * mm});
            skLineSegment(sketch, "E59", {"start": v(-190.5, -368.3) * mm, "end": v(-228.6, -292.1) * mm});
            skLineSegment(sketch, "E60", {"start": v(-228.6, -292.1) * mm, "end": v(-228.6, -104.78) * mm});
            skLineSegment(sketch, "E61", {"start": v(-228.6, -104.78) * mm, "end": v(228.6, -104.78) * mm});
            skSolve(sketch);
        }
        {
            var Q0;
            Q0 = qSketchRegion(id + "F26", true);
            extrude(context, id + "F27", {"entities" : qUnion([Q0]), "depth" : 12.7 * mm});
        }
        {
            var Q0;
            Q0=makeQuery(id+"F20.opPattern","COPY",FACE,{"derivedFrom":makeQuery(id+"F17.opExtrude","CAP_FACE",FACE,{"disambiguationData":[OSD([sQuery(id+"F16.wireOp",EDGE,"E45.bottom"),sQuery(id+"F16.wireOp",EDGE,"E45.top"),sQuery(id+"F16.wireOp",EDGE,"E45.left"),sQuery(id+"F16.wireOp",EDGE,"E45.right")])],"isStart":false}),"instanceName":"1"});
            var sketch = newSketch(context, id + "F28", { "sketchPlane" : qUnion([Q0])});
            skLineSegment(sketch, "E62.bottom", {"start": v(228.6, 73.03) * mm, "end": v(-228.6, 73.02) * mm});
            skLineSegment(sketch, "E62.top", {"start": v(228.6, -101.6) * mm, "end": v(-228.6, -101.6) * mm});
            skLineSegment(sketch, "E62.left", {"start": v(228.6, 73.03) * mm, "end": v(228.6, -101.6) * mm});
            skLineSegment(sketch, "E62.right", {"start": v(-228.6, 73.02) * mm, "end": v(-228.6, -101.6) * mm});
            skSolve(sketch);
        }
        {
            var Q0;
            Q0 = qSketchRegion(id + "F28", true);
            extrude(context, id + "F29", {"entities" : qUnion([Q0]), "depth" : 12.7 * mm});
        }
        {
            var Q0;
            Q0=makeQuery(id+"F20.opPattern","COPY",FACE,{"derivedFrom":makeQuery(id+"F17.opExtrude","SWEPT_FACE",FACE,{"disambiguationData":[OSD([sQuery(id+"F16.wireOp",EDGE,"E46.left")])]}),"instanceName":"1"});
            var sketch = newSketch(context, id + "F30", { "sketchPlane" : qUnion([Q0])});
            skCircle(sketch, "E63", {"center": v(-183.87, 90.34) * mm, "radius": 34 * mm, "construction": true});
            skCircle(sketch, "E64.cCircle", {"center": v(-183.87, 90.34) * mm, "radius": 10.82 * mm, "construction": true});
            skLineSegment(sketch, "E64.0", {"start": v(-204.76, 84.74) * mm, "end": v(-178.27, 111.23) * mm, "construction": true});
            skLineSegment(sketch, "E64.1", {"start": v(-178.27, 111.23) * mm, "end": v(-168.57, 75.04) * mm, "construction": true});
            skLineSegment(sketch, "E64.2", {"start": v(-168.57, 75.04) * mm, "end": v(-204.76, 84.74) * mm, "construction": true});
            skPoint(sketch, "E64.0.midPoint", {"position": v(-191.51, 97.98) * mm});
            skLineSegment(sketch, "E65", {"start": v(-78.1, -26.67) * mm, "end": v(-78.1, 117.07) * mm});
            skLineSegment(sketch, "E66", {"start": v(-78.1, 149.92) * mm, "end": v(-214.7, 149.92) * mm});
            skLineSegment(sketch, "E67", {"start": v(-214.7, 149.92) * mm, "end": v(-217.87, 90.34) * mm});
            skLineSegment(sketch, "E68", {"start": v(-217.87, 90.34) * mm, "end": v(-217.87, -26.67) * mm});
            skLineSegment(sketch, "E69", {"start": v(-217.87, -26.67) * mm, "end": v(-78.1, -26.67) * mm});
            skCircle(sketch, "E70", {"center": v(-183.87, 90.34) * mm, "radius": 7.94 * mm});
            skCircle(sketch, "E71", {"center": v(-178.27, 111.23) * mm, "radius": 3.18 * mm});
            skCircle(sketch, "E72", {"center": v(-168.57, 75.04) * mm, "radius": 3.18 * mm});
            skCircle(sketch, "E73", {"center": v(-204.76, 84.74) * mm, "radius": 3.18 * mm});
            skCircle(sketch, "E74", {"center": v(-104.77, 0) * mm, "radius": 4.95 * mm});
            skLineSegment(sketch, "E75", {"start": v(-104.77, 0) * mm, "end": v(-104.77, 130) * mm, "construction": true});
            skLineSegment(sketch, "E76", {"start": v(-104.78, 0) * mm, "end": v(-86.68, 128.73) * mm, "construction": true});
            skArc(sketch, "E77", {"start": v(-87.37, 123.83) * mm, "mid": v(-81.78, 128.04) * mm, "end": v(-86, 133.63) * mm});
            skArc(sketch, "E78", {"start": v(-123.56, 133.63) * mm, "mid": v(-127.77, 128.04) * mm, "end": v(-122.18, 123.82) * mm});
            skArc(sketch, "E79", {"start": v(-86.68, 128.73) * mm, "mid": v(-104.77, 130) * mm, "end": v(-122.87, 128.73) * mm, "construction": true});
            skArc(sketch, "E80", {"start": v(-86, 133.63) * mm, "mid": v(-104.78, 134.95) * mm, "end": v(-123.56, 133.63) * mm});
            skArc(sketch, "E81", {"start": v(-87.37, 123.82) * mm, "mid": v(-104.78, 125.04) * mm, "end": v(-122.18, 123.82) * mm});
            skLineSegment(sketch, "E82.anchor1", {"start": v(-104.78, 0) * mm, "end": v(-122.18, 123.83) * mm, "construction": true});
            skLineSegment(sketch, "E83", {"start": v(-104.77, 0) * mm, "end": v(-193.67, 0) * mm, "construction": true});
            skArc(sketch, "E84", {"start": v(-192.8, 12.37) * mm, "mid": v(-193.67, 0) * mm, "end": v(-192.8, -12.37) * mm, "construction": true});
            skLineSegment(sketch, "E85", {"start": v(-187.9, 11.68) * mm, "end": v(-104.77, 0) * mm, "construction": true});
            skLineSegment(sketch, "E86.MirrorCS", {"start": v(-187.9, -11.68) * mm, "end": v(-104.77, 0) * mm, "construction": true});
            skArc(sketch, "E87", {"start": v(-187.9, 11.68) * mm, "mid": v(-192.12, 17.28) * mm, "end": v(-197.71, 13.06) * mm});
            skArc(sketch, "E88", {"start": v(-197.71, -13.06) * mm, "mid": v(-192.12, -17.28) * mm, "end": v(-187.9, -11.68) * mm});
            skArc(sketch, "E89", {"start": v(-187.9, 11.68) * mm, "mid": v(-188.72, 0) * mm, "end": v(-187.9, -11.68) * mm});
            skArc(sketch, "E90", {"start": v(-197.71, 13.06) * mm, "mid": v(-198.63, 0) * mm, "end": v(-197.71, -13.06) * mm});
            skLineSegment(sketch, "E91.trimOffspring", {"start": v(-78.1, 140.4) * mm, "end": v(-78.1, 149.92) * mm});
            skArc(sketch, "E92.trimOffspring", {"start": v(-78.1, 117.07) * mm, "mid": v(-72.2, 128.73) * mm, "end": v(-78.1, 140.4) * mm});
            skLineSegment(sketch, "E93.0", {"start": v(-136.52, 31.75) * mm, "end": v(-136.52, 222.25) * mm});
            skLineSegment(sketch, "E93.1", {"start": v(-241.3, 44.45) * mm, "end": v(-141.6, 44.45) * mm});
            skLineSegment(sketch, "E94.1.0", {"start": v(-233.79, 63.02) * mm, "end": v(-135.06, 49.14) * mm, "construction": true});
            skLineSegment(sketch, "E94.anchor1", {"start": v(-104.78, 0) * mm, "end": v(-241.3, 44.45) * mm, "construction": true});
            skLineSegment(sketch, "E94.anchor2", {"start": v(-104.78, 0) * mm, "end": v(-233.79, 63.02) * mm, "construction": true});
            skLineSegment(sketch, "E95.1.0", {"start": v(-140.63, 27.02) * mm, "end": v(-167.15, 215.67) * mm, "construction": true});
            skLineSegment(sketch, "E95.anchor1", {"start": v(-104.78, 0) * mm, "end": v(-136.52, 31.75) * mm, "construction": true});
            skLineSegment(sketch, "E95.anchor2", {"start": v(-104.78, 0) * mm, "end": v(-140.63, 27.02) * mm, "construction": true});
            skSolve(sketch);
        }
        {
            var Q0;
            Q0 = qSketchRegion(id + "F30", true);
            extrude(context, id + "F31", {"entities" : qUnion([Q0]), "depth" : 6.35 * mm});
        }
        {
            var Q0;
            Q0=makeQuery(id+"F31.opExtrude","CAP_FACE",FACE,{"disambiguationData":[OSD([sQuery(id+"F30.wireOp",EDGE,"E65"),sQuery(id+"F30.wireOp",EDGE,"E66"),sQuery(id+"F30.wireOp",EDGE,"E67"),sQuery(id+"F30.wireOp",EDGE,"E68"),sQuery(id+"F30.wireOp",EDGE,"E69"),sQuery(id+"F30.wireOp",EDGE,"E70"),sQuery(id+"F30.wireOp",EDGE,"E71"),sQuery(id+"F30.wireOp",EDGE,"E72"),sQuery(id+"F30.wireOp",EDGE,"E73"),sQuery(id+"F30.wireOp",EDGE,"E74"),sQuery(id+"F30.wireOp",EDGE,"E77"),sQuery(id+"F30.wireOp",EDGE,"E78"),sQuery(id+"F30.wireOp",EDGE,"E80"),sQuery(id+"F30.wireOp",EDGE,"E81"),sQuery(id+"F30.wireOp",EDGE,"E87"),sQuery(id+"F30.wireOp",EDGE,"E88"),sQuery(id+"F30.wireOp",EDGE,"E89"),sQuery(id+"F30.wireOp",EDGE,"E90"),sQuery(id+"F30.wireOp",EDGE,"E91.trimOffspring"),sQuery(id+"F30.wireOp",EDGE,"E92.trimOffspring")])],"isStart":false});
            var sketch = newSketch(context, id + "F32", { "sketchPlane" : qUnion([Q0])});
            skArc(sketch, "E96", {"start": v(-78.1, 140.4) * mm, "mid": v(-82.17, 142.49) * mm, "end": v(-86.68, 143.2) * mm});
            skLineSegment(sketch, "E97", {"start": v(-86.68, 143.2) * mm, "end": v(-122.87, 143.2) * mm});
            skArc(sketch, "E98", {"start": v(-122.87, 143.2) * mm, "mid": v(-127.15, 142.56) * mm, "end": v(-131.04, 140.68) * mm});
            skArc(sketch, "E99", {"start": v(-183.87, 124.34) * mm, "mid": v(-156.22, 128.52) * mm, "end": v(-131.04, 140.68) * mm});
            skArc(sketch, "E100", {"start": v(-183.87, 124.34) * mm, "mid": v(-207.9, 114.38) * mm, "end": v(-217.87, 90.34) * mm});
            skLineSegment(sketch, "E101.0", {"start": v(-217.87, 149.92) * mm, "end": v(-217.87, 90.34) * mm});
            skLineSegment(sketch, "E101.1", {"start": v(-78.1, 149.92) * mm, "end": v(-217.87, 149.92) * mm});
            skLineSegment(sketch, "E101.2", {"start": v(-78.1, 140.4) * mm, "end": v(-78.1, 149.92) * mm});
            skLineSegment(sketch, "E102", {"start": v(-97.15, 104.77) * mm, "end": v(-97.15, 22.76) * mm});
            skLineSegment(sketch, "E103", {"start": v(-97.16, 22.76) * mm, "end": v(-117.05, 104.77) * mm});
            skLineSegment(sketch, "E104", {"start": v(-117.05, 104.77) * mm, "end": v(-97.15, 104.77) * mm});
            skArc(sketch, "E105", {"start": v(-191.69, 40.14) * mm, "mid": v(-150.96, 51.64) * mm, "end": v(-133.07, 89.98) * mm});
            skLineSegment(sketch, "E106", {"start": v(-133.07, 89.98) * mm, "end": v(-112.9, 6.88) * mm});
            skLineSegment(sketch, "E107", {"start": v(-112.9, 6.88) * mm, "end": v(-191.69, 40.14) * mm});
            skLineSegment(sketch, "E108", {"start": v(-127.54, -7.62) * mm, "end": v(-168.86, -7.62) * mm});
            skLineSegment(sketch, "E109", {"start": v(-168.86, -7.62) * mm, "end": v(-168.86, 9.82) * mm});
            skLineSegment(sketch, "E110", {"start": v(-168.86, 9.82) * mm, "end": v(-127.54, -7.62) * mm});
            skLineSegment(sketch, "E111", {"start": v(-183.87, 124.34) * mm, "end": v(-144.85, 124.34) * mm, "construction": true});
            skSolve(sketch);
        }
        {
            var Q0;
            Q0 = qSketchRegion(id + "F32", true);
            extrude(context, id + "F33", {"entities" : qUnion([Q0]), "operationType" : NewBodyOperationType.REMOVE, "endBound" : BoundingType.THROUGH_ALL, "oppositeDirection" : true, "depth" : 25.4 * mm});
        }
        {
            var Q0;
            Q0=makeQuery(id+"F33.boolean.opBoolean","COPY",EDGE,{"derivedFrom":makeQuery(id+"F33.opExtrude","SWEPT_EDGE",EDGE,{"disambiguationData":[OSD([sQuery(id+"F32.wireOp",EDGE,"E105"),sQuery(id+"F32.wireOp",EDGE,"E107")])]})});
            var Q1;
            Q1=makeQuery(id+"F33.boolean.opBoolean","COPY",EDGE,{"derivedFrom":makeQuery(id+"F33.opExtrude","SWEPT_EDGE",EDGE,{"disambiguationData":[OSD([sQuery(id+"F32.wireOp",EDGE,"E105"),sQuery(id+"F32.wireOp",EDGE,"E106")])]})});
            var Q2;
            Q2=makeQuery(id+"F33.boolean.opBoolean","COPY",EDGE,{"derivedFrom":makeQuery(id+"F33.opExtrude","SWEPT_EDGE",EDGE,{"disambiguationData":[OSD([sQuery(id+"F32.wireOp",EDGE,"E103"),sQuery(id+"F32.wireOp",EDGE,"E104")])]})});
            var Q3;
            Q3=makeQuery(id+"F33.boolean.opBoolean","COPY",EDGE,{"derivedFrom":makeQuery(id+"F33.opExtrude","SWEPT_EDGE",EDGE,{"disambiguationData":[OSD([sQuery(id+"F32.wireOp",EDGE,"E102"),sQuery(id+"F32.wireOp",EDGE,"E104")])]})});
            var Q4;
            Q4=makeQuery(id+"F33.boolean.opBoolean","COPY",EDGE,{"derivedFrom":makeQuery(id+"F33.opExtrude","SWEPT_EDGE",EDGE,{"disambiguationData":[OSD([sQuery(id+"F32.wireOp",EDGE,"E102"),sQuery(id+"F32.wireOp",EDGE,"E103")])]})});
            var Q5;
            Q5=makeQuery(id+"F33.boolean.opBoolean","COPY",EDGE,{"derivedFrom":makeQuery(id+"F33.opExtrude","SWEPT_EDGE",EDGE,{"disambiguationData":[OSD([sQuery(id+"F32.wireOp",EDGE,"E106"),sQuery(id+"F32.wireOp",EDGE,"E107")])]})});
            var Q6;
            Q6=makeQuery(id+"F33.boolean.opBoolean","COPY",EDGE,{"derivedFrom":makeQuery(id+"F33.opExtrude","SWEPT_EDGE",EDGE,{"disambiguationData":[OSD([sQuery(id+"F32.wireOp",EDGE,"E108"),sQuery(id+"F32.wireOp",EDGE,"E110")])]})});
            var Q7;
            Q7=makeQuery(id+"F33.boolean.opBoolean","COPY",EDGE,{"derivedFrom":makeQuery(id+"F33.opExtrude","SWEPT_EDGE",EDGE,{"disambiguationData":[OSD([sQuery(id+"F32.wireOp",EDGE,"E109"),sQuery(id+"F32.wireOp",EDGE,"E110")])]})});
            var Q8;
            Q8=makeQuery(id+"F33.boolean.opBoolean","COPY",EDGE,{"derivedFrom":makeQuery(id+"F33.opExtrude","SWEPT_EDGE",EDGE,{"disambiguationData":[OSD([sQuery(id+"F32.wireOp",EDGE,"E108"),sQuery(id+"F32.wireOp",EDGE,"E109")])]})});
            fillet(context, id + "F34", {"entities" : qUnion([Q0, Q1, Q2, Q3, Q4, Q5, Q6, Q7, Q8]), "radius" : 3.3 * mm, "tangentPropagation" : true, "allowEdgeOverflow" : false});
        }
        {
            var Q0;
            {var subQ0=sQuery(id+"F30.wireOp",EDGE,"E68");Q0=makeQuery(id+"F33.boolean.opBoolean","MERGE",EDGE,{"derivedFrom":[makeQuery(id+"F31.opExtrude","SWEPT_EDGE",EDGE,{"disambiguationData":[OSD([sQuery(id+"F30.wireOp",EDGE,"E67"),subQ0])]}),makeQuery(id+"F33.opExtrude","SWEPT_EDGE",EDGE,{"disambiguationData":[OSD([subQ0,sQuery(id+"F32.wireOp",EDGE,"E100"),sQuery(id+"F32.wireOp",EDGE,"E101.0")])]})]});}
            var Q1;
            Q1=makeQuery(id+"F31.opExtrude","SWEPT_EDGE",EDGE,{"disambiguationData":[OSD([sQuery(id+"F16.wireOp",EDGE,"E46.top"),sQuery(id+"F16.wireOp",EDGE,"E46.left"),sQuery(id+"F30.wireOp",EDGE,"E65"),sQuery(id+"F30.wireOp",EDGE,"E92.trimOffspring")])]});
            var Q2;
            Q2=makeQuery(id+"F31.opExtrude","SWEPT_EDGE",EDGE,{"disambiguationData":[OSD([sQuery(id+"F30.wireOp",EDGE,"E65"),sQuery(id+"F30.wireOp",EDGE,"E69")])]});
            var Q3;
            Q3=makeQuery(id+"F31.opExtrude","SWEPT_EDGE",EDGE,{"disambiguationData":[OSD([sQuery(id+"F30.wireOp",EDGE,"E68"),sQuery(id+"F30.wireOp",EDGE,"E69")])]});
            fillet(context, id + "F35", {"entities" : qUnion([Q0, Q1, Q2, Q3]), "radius" : 25.4 * mm, "tangentPropagation" : true, "allowEdgeOverflow" : false});
        }
        {
            var Q0;
            Q0=makeQuery(id+"F31.opExtrude","CAP_FACE",FACE,{"disambiguationData":[OSD([sQuery(id+"F30.wireOp",EDGE,"E65"),sQuery(id+"F30.wireOp",EDGE,"E66"),sQuery(id+"F30.wireOp",EDGE,"E67"),sQuery(id+"F30.wireOp",EDGE,"E68"),sQuery(id+"F30.wireOp",EDGE,"E69"),sQuery(id+"F30.wireOp",EDGE,"E70"),sQuery(id+"F30.wireOp",EDGE,"E71"),sQuery(id+"F30.wireOp",EDGE,"E72"),sQuery(id+"F30.wireOp",EDGE,"E73"),sQuery(id+"F30.wireOp",EDGE,"E74"),sQuery(id+"F30.wireOp",EDGE,"E77"),sQuery(id+"F30.wireOp",EDGE,"E78"),sQuery(id+"F30.wireOp",EDGE,"E80"),sQuery(id+"F30.wireOp",EDGE,"E81"),sQuery(id+"F30.wireOp",EDGE,"E87"),sQuery(id+"F30.wireOp",EDGE,"E88"),sQuery(id+"F30.wireOp",EDGE,"E89"),sQuery(id+"F30.wireOp",EDGE,"E90"),sQuery(id+"F30.wireOp",EDGE,"E91.trimOffspring"),sQuery(id+"F30.wireOp",EDGE,"E92.trimOffspring")])],"isStart":false});
            var sketch = newSketch(context, id + "F36", { "sketchPlane" : qUnion([Q0])});
            skPoint(sketch, "E112", {"position": v(-178.27, 111.23) * mm});
            skPoint(sketch, "E113", {"position": v(-168.57, 75.04) * mm});
            skPoint(sketch, "E114", {"position": v(-204.76, 84.74) * mm});
            skSolve(sketch);
        }
        {
            var Q0;
            Q0=sQuery(id+"F36.wireOp",VERTEX,"E112");
            var Q1;
            Q1=sQuery(id+"F36.wireOp",VERTEX,"E114");
            var Q2;
            Q2=sQuery(id+"F36.wireOp",VERTEX,"E113");
            var Q3;
            Q3=makeQuery(id+"F31.opExtrude","SWEPT_BODY",BODY,{"disambiguationData":[OSD([sQuery(id+"F30.wireOp",EDGE,"E65"),sQuery(id+"F30.wireOp",EDGE,"E66"),sQuery(id+"F30.wireOp",EDGE,"E67"),sQuery(id+"F30.wireOp",EDGE,"E68"),sQuery(id+"F30.wireOp",EDGE,"E69"),sQuery(id+"F30.wireOp",EDGE,"E70"),sQuery(id+"F30.wireOp",EDGE,"E71"),sQuery(id+"F30.wireOp",EDGE,"E72"),sQuery(id+"F30.wireOp",EDGE,"E73"),sQuery(id+"F30.wireOp",EDGE,"E74"),sQuery(id+"F30.wireOp",EDGE,"E77"),sQuery(id+"F30.wireOp",EDGE,"E78"),sQuery(id+"F30.wireOp",EDGE,"E80"),sQuery(id+"F30.wireOp",EDGE,"E81"),sQuery(id+"F30.wireOp",EDGE,"E87"),sQuery(id+"F30.wireOp",EDGE,"E88"),sQuery(id+"F30.wireOp",EDGE,"E89"),sQuery(id+"F30.wireOp",EDGE,"E90"),sQuery(id+"F30.wireOp",EDGE,"E91.trimOffspring"),sQuery(id+"F30.wireOp",EDGE,"E92.trimOffspring")])]});
            hole(context, id + "F37", {"style" : HoleStyle.C_SINK, "holeDiameter" : 6.35 * mm, "cSinkDiameter" : 15.24 * mm, "endStyle" : HoleEndStyle.THROUGH, "locations" : qUnion([Q0, Q1, Q2]), "scope" : qUnion([Q3]), "cSinkAngle" : 90 * degree});
        }
        {
            var Q0;
            Q0=makeQuery(id+"F31.opExtrude","CAP_FACE",FACE,{"disambiguationData":[OSD([sQuery(id+"F30.wireOp",EDGE,"E65"),sQuery(id+"F30.wireOp",EDGE,"E66"),sQuery(id+"F30.wireOp",EDGE,"E67"),sQuery(id+"F30.wireOp",EDGE,"E68"),sQuery(id+"F30.wireOp",EDGE,"E69"),sQuery(id+"F30.wireOp",EDGE,"E70"),sQuery(id+"F30.wireOp",EDGE,"E71"),sQuery(id+"F30.wireOp",EDGE,"E72"),sQuery(id+"F30.wireOp",EDGE,"E73"),sQuery(id+"F30.wireOp",EDGE,"E74"),sQuery(id+"F30.wireOp",EDGE,"E77"),sQuery(id+"F30.wireOp",EDGE,"E78"),sQuery(id+"F30.wireOp",EDGE,"E80"),sQuery(id+"F30.wireOp",EDGE,"E81"),sQuery(id+"F30.wireOp",EDGE,"E87"),sQuery(id+"F30.wireOp",EDGE,"E88"),sQuery(id+"F30.wireOp",EDGE,"E89"),sQuery(id+"F30.wireOp",EDGE,"E90")])],"isStart":false});
            var sketch = newSketch(context, id + "F38", { "sketchPlane" : qUnion([Q0])});
            skCircle(sketch, "E115", {"center": v(-311.15, 0) * mm, "radius": 48 * mm, "construction": true});
            skArc(sketch, "E116", {"start": v(-309.14, 28.72) * mm, "mid": v(-311.15, 0) * mm, "end": v(-309.14, -28.72) * mm, "construction": true});
            skLineSegment(sketch, "E117", {"start": v(-309.14, 28.72) * mm, "end": v(-104.77, 0) * mm, "construction": true});
            skLineSegment(sketch, "E118", {"start": v(-104.77, 0) * mm, "end": v(-309.14, -28.72) * mm, "construction": true});
            skLineSegment(sketch, "E119", {"start": v(-311.15, 0) * mm, "end": v(-104.77, 0) * mm, "construction": true});
            skCircle(sketch, "E120", {"center": v(-309.14, 28.72) * mm, "radius": 48 * mm, "construction": true});
            skCircle(sketch, "E121", {"center": v(-309.14, -28.72) * mm, "radius": 48 * mm, "construction": true});
            skCircle(sketch, "E122", {"center": v(-183.87, 90.34) * mm, "radius": 21.2 * mm, "construction": true});
            skCircle(sketch, "E123", {"center": v(-183.87, 90.34) * mm, "radius": 14.86 * mm, "construction": true});
            skCircle(sketch, "E124", {"center": v(-309.14, 28.72) * mm, "radius": 41.66 * mm, "construction": true});
            skCircle(sketch, "E125", {"center": v(-183.87, 90.34) * mm, "radius": 34 * mm, "construction": true});
            skLineSegment(sketch, "E126", {"start": v(-217.87, 44.45) * mm, "end": v(-78.1, 44.45) * mm, "construction": true});
            skLineSegment(sketch, "E127.1.0", {"start": v(-210.58, 59.76) * mm, "end": v(-72.18, 40.3) * mm, "construction": true});
            skLineSegment(sketch, "E127.anchor1", {"start": v(-104.77, 0) * mm, "end": v(-217.87, 44.45) * mm, "construction": true});
            skLineSegment(sketch, "E127.anchor2", {"start": v(-104.77, 0) * mm, "end": v(-210.58, 59.76) * mm, "construction": true});
            skCircle(sketch, "E128", {"center": v(-309.14, -28.72) * mm, "radius": 41.66 * mm, "construction": true});
            skLineSegment(sketch, "E129", {"start": v(-183.87, 90.34) * mm, "end": v(-189.4, 110.81) * mm, "construction": true});
            skLineSegment(sketch, "E130", {"start": v(-183.87, 90.34) * mm, "end": v(-171.03, 73.46) * mm, "construction": true});
            skLineSegment(sketch, "E131", {"start": v(-280.08, -9.49) * mm, "end": v(-171.03, 73.46) * mm});
            skLineSegment(sketch, "E132", {"start": v(-321.67, 75.07) * mm, "end": v(-189.4, 110.81) * mm});
            skLineSegment(sketch, "E133", {"start": v(-336.42, 10.78) * mm, "end": v(-195.92, 107.79) * mm});
            skLineSegment(sketch, "E134", {"start": v(-167.05, 77.41) * mm, "end": v(-271.07, -57.97) * mm});
            skSolve(sketch);
        }
        {
            var Q0;
            Q0=makeQuery(id+"F31.opExtrude","CAP_FACE",FACE,{"disambiguationData":[OSD([sQuery(id+"F30.wireOp",EDGE,"E65"),sQuery(id+"F30.wireOp",EDGE,"E66"),sQuery(id+"F30.wireOp",EDGE,"E67"),sQuery(id+"F30.wireOp",EDGE,"E68"),sQuery(id+"F30.wireOp",EDGE,"E69"),sQuery(id+"F30.wireOp",EDGE,"E70"),sQuery(id+"F30.wireOp",EDGE,"E71"),sQuery(id+"F30.wireOp",EDGE,"E72"),sQuery(id+"F30.wireOp",EDGE,"E73"),sQuery(id+"F30.wireOp",EDGE,"E74"),sQuery(id+"F30.wireOp",EDGE,"E77"),sQuery(id+"F30.wireOp",EDGE,"E78"),sQuery(id+"F30.wireOp",EDGE,"E80"),sQuery(id+"F30.wireOp",EDGE,"E81"),sQuery(id+"F30.wireOp",EDGE,"E87"),sQuery(id+"F30.wireOp",EDGE,"E88"),sQuery(id+"F30.wireOp",EDGE,"E89"),sQuery(id+"F30.wireOp",EDGE,"E90"),sQuery(id+"F30.wireOp",EDGE,"E91.trimOffspring"),sQuery(id+"F30.wireOp",EDGE,"E92.trimOffspring")])],"isStart":true});
            var sketch = newSketch(context, id + "F39", { "sketchPlane" : qUnion([Q0])});
            skLineSegment(sketch, "E135", {"start": v(183.87, 124.34) * mm, "end": v(207.18, 128.41) * mm});
            skArc(sketch, "E136", {"start": v(214.59, 122.83) * mm, "mid": v(212.1, 127.23) * mm, "end": v(207.18, 128.41) * mm});
            skLineSegment(sketch, "E137", {"start": v(214.59, 122.83) * mm, "end": v(217.67, 93.95) * mm});
            skArc(sketch, "E138.0", {"start": v(183.87, 124.34) * mm, "mid": v(206.6, 115.62) * mm, "end": v(217.67, 93.95) * mm});
            skSolve(sketch);
        }
        {
            var Q0;
            Q0 = qSketchRegion(id + "F39", true);
            var Q1;
            Q1=makeQuery(id+"F31.opExtrude","CAP_FACE",FACE,{"disambiguationData":[OSD([sQuery(id+"F30.wireOp",EDGE,"E65"),sQuery(id+"F30.wireOp",EDGE,"E66"),sQuery(id+"F30.wireOp",EDGE,"E67"),sQuery(id+"F30.wireOp",EDGE,"E68"),sQuery(id+"F30.wireOp",EDGE,"E69"),sQuery(id+"F30.wireOp",EDGE,"E70"),sQuery(id+"F30.wireOp",EDGE,"E71"),sQuery(id+"F30.wireOp",EDGE,"E72"),sQuery(id+"F30.wireOp",EDGE,"E73"),sQuery(id+"F30.wireOp",EDGE,"E74"),sQuery(id+"F30.wireOp",EDGE,"E77"),sQuery(id+"F30.wireOp",EDGE,"E78"),sQuery(id+"F30.wireOp",EDGE,"E80"),sQuery(id+"F30.wireOp",EDGE,"E81"),sQuery(id+"F30.wireOp",EDGE,"E87"),sQuery(id+"F30.wireOp",EDGE,"E88"),sQuery(id+"F30.wireOp",EDGE,"E89"),sQuery(id+"F30.wireOp",EDGE,"E90"),sQuery(id+"F30.wireOp",EDGE,"E91.trimOffspring"),sQuery(id+"F30.wireOp",EDGE,"E92.trimOffspring")])],"isStart":false});
            extrude(context, id + "F40", {"entities" : qUnion([Q0]), "operationType" : NewBodyOperationType.ADD, "endBound" : BoundingType.UP_TO_SURFACE, "oppositeDirection" : true, "endBoundEntityFace" : qUnion([Q1]), "depth" : 25.4 * mm});
        }
        {
            var Q0;
            Q0=makeQuery(id+"F40.boolean.opBoolean","MERGE",FACE,{"derivedFrom":[makeQuery(id+"F31.opExtrude","CAP_FACE",FACE,{"disambiguationData":[OSD([sQuery(id+"F30.wireOp",EDGE,"E65"),sQuery(id+"F30.wireOp",EDGE,"E66"),sQuery(id+"F30.wireOp",EDGE,"E67"),sQuery(id+"F30.wireOp",EDGE,"E68"),sQuery(id+"F30.wireOp",EDGE,"E69"),sQuery(id+"F30.wireOp",EDGE,"E70"),sQuery(id+"F30.wireOp",EDGE,"E71"),sQuery(id+"F30.wireOp",EDGE,"E72"),sQuery(id+"F30.wireOp",EDGE,"E73"),sQuery(id+"F30.wireOp",EDGE,"E74"),sQuery(id+"F30.wireOp",EDGE,"E77"),sQuery(id+"F30.wireOp",EDGE,"E78"),sQuery(id+"F30.wireOp",EDGE,"E80"),sQuery(id+"F30.wireOp",EDGE,"E81"),sQuery(id+"F30.wireOp",EDGE,"E87"),sQuery(id+"F30.wireOp",EDGE,"E88"),sQuery(id+"F30.wireOp",EDGE,"E89"),sQuery(id+"F30.wireOp",EDGE,"E90"),sQuery(id+"F30.wireOp",EDGE,"E91.trimOffspring"),sQuery(id+"F30.wireOp",EDGE,"E92.trimOffspring")])],"isStart":true}),makeQuery(id+"F40.opExtrude","CAP_FACE",FACE,{"disambiguationData":[OSD([sQuery(id+"F39.wireOp",EDGE,"E135"),sQuery(id+"F39.wireOp",EDGE,"E136"),sQuery(id+"F39.wireOp",EDGE,"E137"),sQuery(id+"F39.wireOp",EDGE,"E138.0")])],"isStart":true})]});
            var sketch = newSketch(context, id + "F41", { "sketchPlane" : qUnion([Q0])});
            skPoint(sketch, "E139", {"position": v(208.27, 122.15) * mm});
            skPoint(sketch, "E140", {"position": v(144.06, 95.17) * mm});
            skPoint(sketch, "E141", {"position": v(208.27, 68.18) * mm});
            skCircle(sketch, "E142", {"center": v(183.87, 90.34) * mm, "radius": 40.1 * mm, "construction": true});
            skLineSegment(sketch, "E143", {"start": v(208.27, 122.15) * mm, "end": v(208.27, 68.18) * mm, "construction": true});
            skLineSegment(sketch, "E144", {"start": v(208.27, 95.17) * mm, "end": v(144.06, 95.17) * mm, "construction": true});
            skSolve(sketch);
        }
        {
            var Q0;
            Q0=sQuery(id+"F41.wireOp",VERTEX,"E139");
            var Q1;
            Q1=sQuery(id+"F41.wireOp",VERTEX,"E141");
            var Q2;
            Q2=sQuery(id+"F41.wireOp",VERTEX,"E140");
            var Q3;
            Q3=makeQuery(id+"F31.opExtrude","SWEPT_BODY",BODY,{"disambiguationData":[OSD([sQuery(id+"F30.wireOp",EDGE,"E65"),sQuery(id+"F30.wireOp",EDGE,"E66"),sQuery(id+"F30.wireOp",EDGE,"E67"),sQuery(id+"F30.wireOp",EDGE,"E68"),sQuery(id+"F30.wireOp",EDGE,"E69"),sQuery(id+"F30.wireOp",EDGE,"E70"),sQuery(id+"F30.wireOp",EDGE,"E71"),sQuery(id+"F30.wireOp",EDGE,"E72"),sQuery(id+"F30.wireOp",EDGE,"E73"),sQuery(id+"F30.wireOp",EDGE,"E74"),sQuery(id+"F30.wireOp",EDGE,"E77"),sQuery(id+"F30.wireOp",EDGE,"E78"),sQuery(id+"F30.wireOp",EDGE,"E80"),sQuery(id+"F30.wireOp",EDGE,"E81"),sQuery(id+"F30.wireOp",EDGE,"E87"),sQuery(id+"F30.wireOp",EDGE,"E88"),sQuery(id+"F30.wireOp",EDGE,"E89"),sQuery(id+"F30.wireOp",EDGE,"E90"),sQuery(id+"F30.wireOp",EDGE,"E91.trimOffspring"),sQuery(id+"F30.wireOp",EDGE,"E92.trimOffspring")])]});
            hole(context, id + "F42", {"style" : HoleStyle.C_SINK, "holeDiameter" : 4.64 * mm, "cSinkDiameter" : 9.12 * mm, "endStyle" : HoleEndStyle.THROUGH, "locations" : qUnion([Q0, Q1, Q2]), "scope" : qUnion([Q3]), "cSinkAngle" : 90 * degree});
        }
        {
            var Q0;
            {var subQ4=sQuery(id+"F30.wireOp",EDGE,"E70");Q0=makeQuery(id+"F38.imprint","IMPRINT",FACE,{"disambiguationData":[TD([[makeQuery(id+"F38.imprint","IMPRINT",EDGE,{"derivedFrom":makeQuery(id+"F31.opExtrude","CAP_EDGE",EDGE,{"disambiguationData":[OSD([subQ4])],"isStart":false})}),-1.0]])]});}
            var sketch = newSketch(context, id + "F43", { "sketchPlane" : qUnion([Q0])});
            skCircle(sketch, "E145", {"center": v(-208.27, 122.15) * mm, "radius": 3.97 * mm});
            skCircle(sketch, "E146", {"center": v(-144.06, 95.17) * mm, "radius": 3.97 * mm});
            skCircle(sketch, "E147", {"center": v(-208.27, 68.18) * mm, "radius": 3.97 * mm});
            skCircle(sketch, "E148.0", {"center": v(-208.27, 68.18) * mm, "radius": 2.32 * mm});
            skCircle(sketch, "E148.1", {"center": v(-208.27, 122.15) * mm, "radius": 2.32 * mm});
            skCircle(sketch, "E148.2", {"center": v(-144.06, 95.17) * mm, "radius": 2.32 * mm});
            skSolve(sketch);
        }
        {
            var Q0;
            Q0 = qSketchRegion(id + "F43", true);
            extrude(context, id + "F44", {"entities" : qUnion([Q0]), "depth" : 31.75 * mm});
        }
        {
            var Q0;
            Q0=makeQuery(id+"F44.opExtrude","CAP_FACE",FACE,{"disambiguationData":[OSD([sQuery(id+"F43.wireOp",EDGE,"E145"),sQuery(id+"F43.wireOp",EDGE,"E148.1")])],"isStart":false});
            var sketch = newSketch(context, id + "F45", { "sketchPlane" : qUnion([Q0])});
            skArc(sketch, "E149", {"start": v(-205.81, 128) * mm, "mid": v(-211.79, 127.44) * mm, "end": v(-214.62, 122.15) * mm});
            skArc(sketch, "E150", {"start": v(-141.6, 89.31) * mm, "mid": v(-137.7, 95.17) * mm, "end": v(-141.6, 101.02) * mm});
            skArc(sketch, "E151", {"start": v(-214.62, 68.18) * mm, "mid": v(-211.79, 62.9) * mm, "end": v(-205.81, 62.33) * mm});
            skLineSegment(sketch, "E152", {"start": v(-205.81, 128) * mm, "end": v(-141.6, 101.02) * mm});
            skLineSegment(sketch, "E153", {"start": v(-214.62, 122.15) * mm, "end": v(-214.62, 68.18) * mm});
            skLineSegment(sketch, "E154", {"start": v(-205.81, 62.33) * mm, "end": v(-141.6, 89.31) * mm});
            skCircle(sketch, "E155.0", {"center": v(-208.27, 122.15) * mm, "radius": 2.32 * mm});
            skCircle(sketch, "E156.0", {"center": v(-144.06, 95.17) * mm, "radius": 2.32 * mm});
            skCircle(sketch, "E157.0", {"center": v(-208.27, 68.18) * mm, "radius": 2.32 * mm});
            skCircle(sketch, "E158", {"center": v(-183.87, 90.34) * mm, "radius": 5 * mm});
            skCircle(sketch, "E159", {"center": v(-192.37, 90.34) * mm, "radius": 0.8 * mm});
            skCircle(sketch, "E160", {"center": v(-175.37, 90.34) * mm, "radius": 0.8 * mm});
            skCircle(sketch, "E161", {"center": v(-183.87, 90.34) * mm, "radius": 8.5 * mm, "construction": true});
            skLineSegment(sketch, "E162", {"start": v(-192.37, 90.34) * mm, "end": v(-175.37, 90.34) * mm, "construction": true});
            skSolve(sketch);
        }
        {
            var Q0;
            Q0 = qSketchRegion(id + "F45", true);
            extrude(context, id + "F46", {"entities" : qUnion([Q0]), "depth" : 6.35 * mm});
        }
    });
